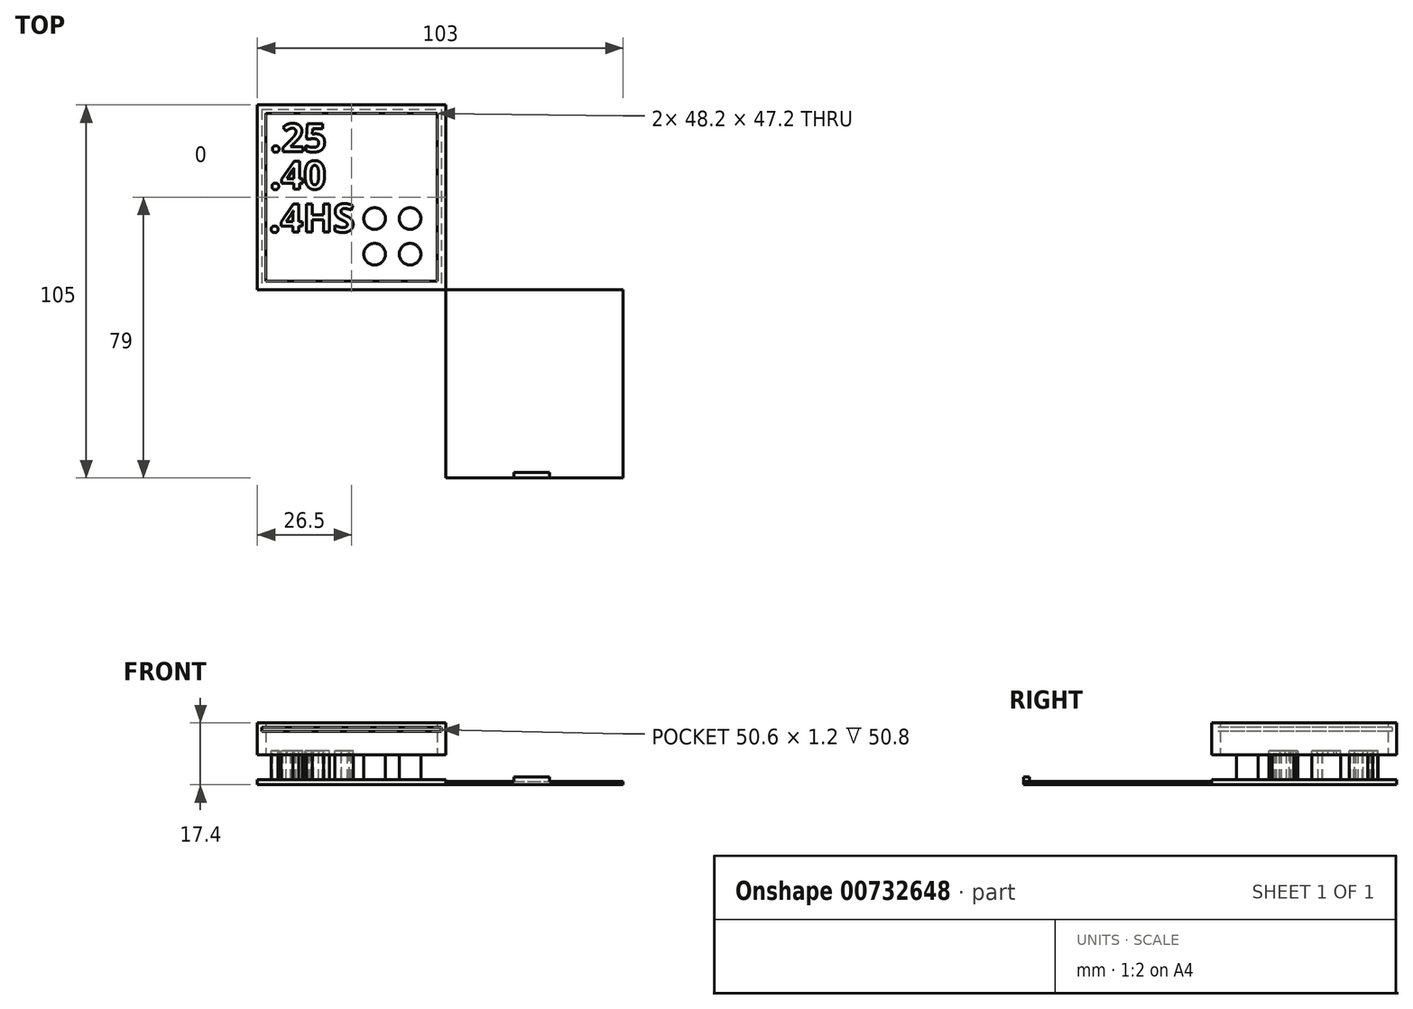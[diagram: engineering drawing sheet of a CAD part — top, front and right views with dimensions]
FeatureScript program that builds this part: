
annotation { "Feature Type Name" : "Feature", "Feature Type Description" : "" }
export const myFeature = defineFeature(function(context is Context, id is Id, definition is map)
    precondition{}
    {
        {
            var Q0;
            Q0=qCreatedBy(makeId("Top.planeOp"),FACE);
            var sketch = newSketch(context, id + "F0", { "sketchPlane" : qUnion([Q0])});
            skLineSegment(sketch, "E0.bottom", {"start": v(0, 0) * mm, "end": v(-53, 0) * mm});
            skLineSegment(sketch, "E0.top", {"start": v(0, 52) * mm, "end": v(-53, 52) * mm});
            skLineSegment(sketch, "E0.left", {"start": v(0, 0) * mm, "end": v(0, 52) * mm});
            skLineSegment(sketch, "E0.right", {"start": v(-53, 0) * mm, "end": v(-53, 52) * mm});
            skSolve(sketch);
        }
        {
            var Q0;
            Q0=makeQuery(id+"F0.imprint","IMPRINT",FACE,{"disambiguationData":[TD([[makeQuery(id+"F0.imprint","IMPRINT",EDGE,{"derivedFrom":sQuery(id+"F0.wireOp",EDGE,"E0.bottom")}),-1.0]])]});
            extrude(context, id + "F1", {"entities" : qUnion([Q0]), "depth" : 8.4 * mm, "offsetDistance" : 25 * mm});
        }
        {
            var Q0;
            Q0=makeQuery(id+"F1.opExtrude","CAP_FACE",FACE,{"disambiguationData":[OSD([sQuery(id+"F0.wireOp",EDGE,"E0.bottom"),sQuery(id+"F0.wireOp",EDGE,"E0.top"),sQuery(id+"F0.wireOp",EDGE,"E0.left"),sQuery(id+"F0.wireOp",EDGE,"E0.right")])],"isStart":false});
            var sketch = newSketch(context, id + "F2", { "sketchPlane" : qUnion([Q0])});
            skLineSegment(sketch, "E1.bottom", {"start": v(0, 0) * mm, "end": v(-53, 0) * mm});
            skLineSegment(sketch, "E1.top", {"start": v(0, 52) * mm, "end": v(-53, 52) * mm});
            skLineSegment(sketch, "E1.left", {"start": v(0, 0) * mm, "end": v(0, 52) * mm});
            skLineSegment(sketch, "E1.right", {"start": v(-53, 0) * mm, "end": v(-53, 52) * mm});
            skLineSegment(sketch, "E2", {"start": v(-53, 42) * mm, "end": v(0, 42) * mm, "construction": true});
            skCircle(sketch, "E3", {"center": v(-10, 42) * mm, "radius": 3.05 * mm});
            skCircle(sketch, "E4", {"center": v(-20, 42) * mm, "radius": 3.05 * mm});
            skLineSegment(sketch, "E5", {"start": v(-53, 32) * mm, "end": v(0, 32) * mm, "construction": true});
            skCircle(sketch, "E6", {"center": v(-20, 32) * mm, "radius": 3.05 * mm});
            skCircle(sketch, "E7", {"center": v(-10, 32) * mm, "radius": 3.05 * mm});
            skLineSegment(sketch, "E8", {"start": v(-10, 52) * mm, "end": v(-10, 0) * mm, "construction": true});
            skLineSegment(sketch, "E9", {"start": v(-20, 52) * mm, "end": v(-20, 0) * mm, "construction": true});
            skLineSegment(sketch, "E10", {"start": v(-53, 26) * mm, "end": v(0, 26) * mm, "construction": true});
            skCircle(sketch, "E11.MirrorC", {"center": v(-20, 20) * mm, "radius": 3.05 * mm});
            skCircle(sketch, "E12.MirrorC", {"center": v(-10, 20) * mm, "radius": 3.05 * mm});
            skCircle(sketch, "E13.MirrorC", {"center": v(-10, 10) * mm, "radius": 3.05 * mm});
            skCircle(sketch, "E14.MirrorC", {"center": v(-20, 10) * mm, "radius": 3.05 * mm});
            skText(sketch, "E15", { "text": ".25", "fontName": "OpenSans-Bold.ttf"});
            skText(sketch, "E16", { "text": ".40", "fontName": "OpenSans-Bold.ttf"});
            skText(sketch, "E17", { "text": ".4HS", "fontName": "OpenSans-Bold.ttf"});
            const initialGuessF2  = {"E15": [-0.04941, 0.0388, 1, 0, 0.008], "E16": [-0.04953, 0.02829, 1, 0, 0.008], "E17": [-0.04973, 0.0162, 1, 0, 0.008]};
            skSetInitialGuess(sketch, initialGuessF2);
            skSolve(sketch);
        }
        {
            var Q0;
            Q0=makeQuery(id+"F2.imprint","IMPRINT",FACE,{"disambiguationData":[TD([[makeQuery(id+"F2.imprint","IMPRINT",EDGE,{"derivedFrom":sQuery(id+"F2.wireOp",EDGE,"E4")}),1.0]])]});
            var Q1;
            Q1=makeQuery(id+"F2.imprint","IMPRINT",FACE,{"disambiguationData":[TD([[makeQuery(id+"F2.imprint","IMPRINT",EDGE,{"derivedFrom":sQuery(id+"F2.wireOp",EDGE,"E3")}),1.0]])]});
            var Q2;
            Q2=makeQuery(id+"F2.imprint","IMPRINT",FACE,{"disambiguationData":[TD([[makeQuery(id+"F2.imprint","IMPRINT",EDGE,{"derivedFrom":sQuery(id+"F2.wireOp",EDGE,"E7")}),1.0]])]});
            var Q3;
            Q3=makeQuery(id+"F2.imprint","IMPRINT",FACE,{"disambiguationData":[TD([[makeQuery(id+"F2.imprint","IMPRINT",EDGE,{"derivedFrom":sQuery(id+"F2.wireOp",EDGE,"E6")}),1.0]])]});
            var Q4;
            Q4=makeQuery(id+"F2.imprint","IMPRINT",FACE,{"disambiguationData":[TD([[makeQuery(id+"F2.imprint","IMPRINT",EDGE,{"derivedFrom":sQuery(id+"F2.wireOp",EDGE,"E11.MirrorC")}),-1.0]])]});
            var Q5;
            Q5=makeQuery(id+"F2.imprint","IMPRINT",FACE,{"disambiguationData":[TD([[makeQuery(id+"F2.imprint","IMPRINT",EDGE,{"derivedFrom":sQuery(id+"F2.wireOp",EDGE,"E12.MirrorC")}),-1.0]])]});
            var Q6;
            Q6=makeQuery(id+"F2.imprint","IMPRINT",FACE,{"disambiguationData":[TD([[makeQuery(id+"F2.imprint","IMPRINT",EDGE,{"derivedFrom":sQuery(id+"F2.wireOp",EDGE,"E13.MirrorC")}),-1.0]])]});
            var Q7;
            Q7=makeQuery(id+"F2.imprint","IMPRINT",FACE,{"disambiguationData":[TD([[makeQuery(id+"F2.imprint","IMPRINT",EDGE,{"derivedFrom":sQuery(id+"F2.wireOp",EDGE,"E14.MirrorC")}),-1.0]])]});
            extrude(context, id + "F3", {"entities" : qUnion([Q0, Q1, Q2, Q3, Q4, Q5, Q6, Q7]), "operationType" : NewBodyOperationType.REMOVE, "oppositeDirection" : true, "depth" : 7 * mm, "offsetDistance" : 25 * mm});
        }
        {
            var Q0;
            Q0=makeQuery(id+"F2.imprint","IMPRINT",FACE,{"disambiguationData":[TD([[makeQuery(id+"F2.imprint","IMPRINT",EDGE,{"derivedFrom":sQuery(id+"F2.wireOp",EDGE,"E17.sketch_text.stroke-38")}),-1.0]])]});
            var Q1;
            Q1=makeQuery(id+"F2.imprint","IMPRINT",FACE,{"disambiguationData":[TD([[makeQuery(id+"F2.imprint","IMPRINT",EDGE,{"derivedFrom":sQuery(id+"F2.wireOp",EDGE,"E17.sketch_text.stroke-26")}),-1.0]])]});
            var Q2;
            Q2=makeQuery(id+"F2.imprint","IMPRINT",FACE,{"disambiguationData":[TD([[makeQuery(id+"F2.imprint","IMPRINT",EDGE,{"derivedFrom":sQuery(id+"F2.wireOp",EDGE,"E17.sketch_text.stroke-8")}),-1.0]])]});
            var Q3;
            Q3=makeQuery(id+"F2.imprint","IMPRINT",FACE,{"disambiguationData":[TD([[makeQuery(id+"F2.imprint","IMPRINT",EDGE,{"derivedFrom":sQuery(id+"F2.wireOp",EDGE,"E17.sketch_text.stroke-0")}),-1.0]])]});
            var Q4;
            Q4=makeQuery(id+"F2.imprint","IMPRINT",FACE,{"disambiguationData":[TD([[makeQuery(id+"F2.imprint","IMPRINT",EDGE,{"derivedFrom":sQuery(id+"F2.wireOp",EDGE,"E16.sketch_text.stroke-0")}),-1.0]])]});
            var Q5;
            Q5=makeQuery(id+"F2.imprint","IMPRINT",FACE,{"disambiguationData":[TD([[makeQuery(id+"F2.imprint","IMPRINT",EDGE,{"derivedFrom":sQuery(id+"F2.wireOp",EDGE,"E16.sketch_text.stroke-8")}),-1.0]])]});
            var Q6;
            Q6=makeQuery(id+"F2.imprint","IMPRINT",FACE,{"disambiguationData":[TD([[makeQuery(id+"F2.imprint","IMPRINT",EDGE,{"derivedFrom":sQuery(id+"F2.wireOp",EDGE,"E16.sketch_text.stroke-26")}),-1.0]])]});
            var Q7;
            Q7=makeQuery(id+"F2.imprint","IMPRINT",FACE,{"disambiguationData":[TD([[makeQuery(id+"F2.imprint","IMPRINT",EDGE,{"derivedFrom":sQuery(id+"F2.wireOp",EDGE,"E15.sketch_text.stroke-32")}),-1.0]])]});
            var Q8;
            Q8=makeQuery(id+"F2.imprint","IMPRINT",FACE,{"disambiguationData":[TD([[makeQuery(id+"F2.imprint","IMPRINT",EDGE,{"derivedFrom":sQuery(id+"F2.wireOp",EDGE,"E15.sketch_text.stroke-8")}),-1.0]])]});
            var Q9;
            Q9=makeQuery(id+"F2.imprint","IMPRINT",FACE,{"disambiguationData":[TD([[makeQuery(id+"F2.imprint","IMPRINT",EDGE,{"derivedFrom":sQuery(id+"F2.wireOp",EDGE,"E15.sketch_text.stroke-0")}),-1.0]])]});
            extrude(context, id + "F4", {"entities" : qUnion([Q0, Q1, Q2, Q3, Q4, Q5, Q6, Q7, Q8, Q9]), "operationType" : NewBodyOperationType.ADD, "depth" : 1.2 * mm, "offsetDistance" : 25 * mm});
        }
        {
            var Q0;
            {var subQ0=sQuery(id+"F0.wireOp",EDGE,"E0.left");var subQ1=sQuery(id+"F0.wireOp",EDGE,"E0.top");var subQ2=sQuery(id+"F0.wireOp",EDGE,"E0.right");var subQ3=sQuery(id+"F0.wireOp",EDGE,"E0.bottom");Q0=makeQuery(id+"F4.boolean.opBoolean","SPLIT",FACE,{"disambiguationData":[TD([makeQuery(id+"F1.opExtrude","SWEPT_FACE",FACE,{"disambiguationData":[OSD([subQ3])]})])],"derivedFrom":makeQuery(id+"F1.opExtrude","CAP_FACE",FACE,{"disambiguationData":[OSD([subQ3,subQ1,subQ0,subQ2])],"isStart":false})});}
            var sketch = newSketch(context, id + "F5", { "sketchPlane" : qUnion([Q0])});
            skLineSegment(sketch, "E18.bottom", {"start": v(0, 0) * mm, "end": v(-53, 0) * mm});
            skLineSegment(sketch, "E18.top", {"start": v(0, 52) * mm, "end": v(-53, 52) * mm});
            skLineSegment(sketch, "E18.left", {"start": v(0, 0) * mm, "end": v(0, 52) * mm});
            skLineSegment(sketch, "E18.right", {"start": v(-53, 0) * mm, "end": v(-53, 52) * mm});
            skLineSegment(sketch, "E19.bottom", {"start": v(-2.4, 2.4) * mm, "end": v(-50.6, 2.4) * mm});
            skLineSegment(sketch, "E19.top", {"start": v(-2.4, 49.6) * mm, "end": v(-50.6, 49.6) * mm});
            skLineSegment(sketch, "E19.left", {"start": v(-2.4, 2.4) * mm, "end": v(-2.4, 49.6) * mm});
            skLineSegment(sketch, "E19.right", {"start": v(-50.6, 2.4) * mm, "end": v(-50.6, 49.6) * mm});
            skSolve(sketch);
        }
        {
            var Q0;
            Q0=makeQuery(id+"F5.imprint","IMPRINT",FACE,{"disambiguationData":[TD([[makeQuery(id+"F5.imprint","IMPRINT",EDGE,{"derivedFrom":sQuery(id+"F5.wireOp",EDGE,"E18.bottom")}),-1.0]])]});
            extrude(context, id + "F6", {"entities" : qUnion([Q0]), "operationType" : NewBodyOperationType.ADD, "depth" : 9 * mm, "offsetDistance" : 25 * mm});
        }
        {
            var Q0;
            Q0=makeQuery(id+"F6.boolean.opBoolean","MERGE",FACE,{"derivedFrom":[makeQuery(id+"F1.opExtrude","SWEPT_FACE",FACE,{"disambiguationData":[OSD([sQuery(id+"F0.wireOp",EDGE,"E0.bottom")])]}),makeQuery(id+"F6.opExtrude","SWEPT_FACE",FACE,{"disambiguationData":[OSD([sQuery(id+"F5.wireOp",EDGE,"E18.bottom")])]})]});
            var sketch = newSketch(context, id + "F7", { "sketchPlane" : qUnion([Q0])});
            skLineSegment(sketch, "E20.bottom", {"start": v(-51.8, 16.2) * mm, "end": v(-1.2, 16.2) * mm});
            skLineSegment(sketch, "E20.top", {"start": v(-51.8, 15) * mm, "end": v(-1.2, 15) * mm});
            skLineSegment(sketch, "E20.left", {"start": v(-51.8, 16.2) * mm, "end": v(-51.8, 15) * mm});
            skLineSegment(sketch, "E20.right", {"start": v(-1.2, 16.2) * mm, "end": v(-1.2, 15) * mm});
            skSolve(sketch);
        }
        {
            var Q0;
            Q0=makeQuery(id+"F7.imprint","IMPRINT",FACE,{"disambiguationData":[TD([[makeQuery(id+"F7.imprint","IMPRINT",EDGE,{"derivedFrom":sQuery(id+"F7.wireOp",EDGE,"E20.bottom")}),-1.0]])]});
            extrude(context, id + "F8", {"entities" : qUnion([Q0]), "operationType" : NewBodyOperationType.REMOVE, "oppositeDirection" : true, "depth" : 50.8 * mm, "offsetDistance" : 25 * mm});
        }
        {
            var Q0;
            Q0=qCreatedBy(makeId("Top.planeOp"),FACE);
            var sketch = newSketch(context, id + "F9", { "sketchPlane" : qUnion([Q0])});
            skLineSegment(sketch, "E21.bottom", {"start": v(0, 0) * mm, "end": v(50, 0) * mm});
            skLineSegment(sketch, "E21.top", {"start": v(0, -53) * mm, "end": v(50, -53) * mm});
            skLineSegment(sketch, "E21.left", {"start": v(0, 0) * mm, "end": v(0, -53) * mm});
            skLineSegment(sketch, "E21.right", {"start": v(50, 0) * mm, "end": v(50, -53) * mm});
            skSolve(sketch);
        }
        {
            var Q0;
            Q0=makeQuery(id+"F9.imprint","IMPRINT",FACE,{"disambiguationData":[TD([[makeQuery(id+"F9.imprint","IMPRINT",EDGE,{"derivedFrom":sQuery(id+"F9.wireOp",EDGE,"E21.bottom")}),-1.0]])]});
            extrude(context, id + "F10", {"entities" : qUnion([Q0]), "depth" : 1 * mm, "offsetDistance" : 25 * mm});
        }
        {
            var Q0;
            Q0=makeQuery(id+"F10.opExtrude","CAP_FACE",FACE,{"disambiguationData":[OSD([sQuery(id+"F9.wireOp",EDGE,"E21.bottom"),sQuery(id+"F9.wireOp",EDGE,"E21.top"),sQuery(id+"F9.wireOp",EDGE,"E21.left"),sQuery(id+"F9.wireOp",EDGE,"E21.right")])],"isStart":false});
            var sketch = newSketch(context, id + "F11", { "sketchPlane" : qUnion([Q0])});
            skLineSegment(sketch, "E22.bottom", {"start": v(19.25, -51.4) * mm, "end": v(29.25, -51.4) * mm});
            skLineSegment(sketch, "E22.top", {"start": v(19.25, -53) * mm, "end": v(29.25, -53) * mm});
            skLineSegment(sketch, "E22.left", {"start": v(19.25, -51.4) * mm, "end": v(19.25, -53) * mm});
            skLineSegment(sketch, "E22.right", {"start": v(29.25, -51.4) * mm, "end": v(29.25, -53) * mm});
            skSolve(sketch);
        }
        {
            var Q0;
            Q0=makeQuery(id+"F11.imprint","IMPRINT",FACE,{"disambiguationData":[TD([[makeQuery(id+"F11.imprint","IMPRINT",EDGE,{"derivedFrom":sQuery(id+"F11.wireOp",EDGE,"E22.bottom")}),-1.0]])]});
            extrude(context, id + "F12", {"entities" : qUnion([Q0]), "operationType" : NewBodyOperationType.ADD, "depth" : 1.2 * mm, "offsetDistance" : 25 * mm});
        }
    });
